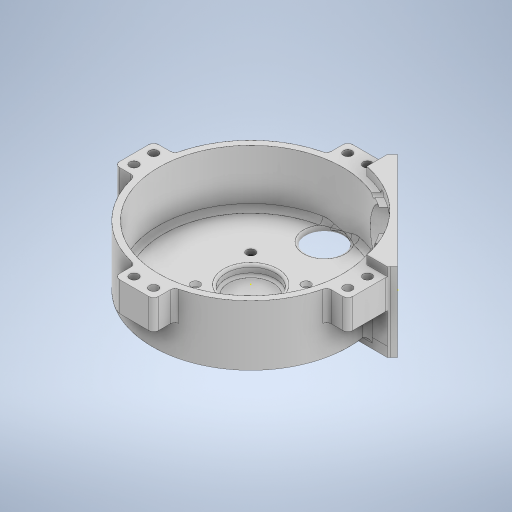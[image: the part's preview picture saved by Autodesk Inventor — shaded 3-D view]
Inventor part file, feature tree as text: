
AUTODESK INVENTOR PART (.ipt)
format: ipt  version: 2023 (Build 270158000, 158)  size: 803,840 bytes
history: native  units: in
note: dims shown in document units (in); Inventor stores cm internally (conversion verified against a paired STEP export)
features: sketch x26, extrude x21, fillet x11, hole x3
ambient origin geometry x8: Origin, YZ Plane, XZ Plane, XY Plane, X Axis, Y Axis, Z Axis, Center Point
bodies: Solid1 (feature_tree)
feature tree (61):
  extrude  "Extrusion1"  Depth=1.375in TaperAngle=0.0deg
  extrude  "Extrusion2"  Depth=1.275in TaperAngle=0.0deg
  extrude  "Extrusion3"  Depth=1.125in TaperAngle=0.0deg
  hole  "Hole1"  [1 undecoded]
  extrude  "Extrusion4"  Depth=0.4in
  extrude  "Extrusion5"  Depth=0.4in
  hole  "Hole2"  [1 undecoded]
  extrude  "Extrusion6"  Depth=0.4in
  sketch  "Sketch10"  dims[d26=0.8in d27=0.4in]
  extrude  "Extrusion7"  Depth=0.4in
  extrude  "Extrusion8"  Depth=0.8in
  extrude  "Extrusion9"  Depth=0.4in
  extrude  "Extrusion18"  Depth=0.75in TaperAngle=0.0deg
  extrude  "Extrusion19"  Depth=0.2in
  extrude  "Extrusion20"  Depth=0.2in
  extrude  "Extrusion21"  Depth=0.4in
  extrude  "Extrusion22"  Depth=0.2in
  extrude  "Extrusion23"  Depth=0.2in
  sketch  "Sketch34"  dims[d125=0.3in d126=0.3in]
  hole  "Hole6"  [1 undecoded]
  extrude  "Extrusion24"  Depth=2.0in TaperAngle=0.0deg
  fillet  "Fillet1"  Radius=2.0in
  fillet  "Fillet2"  Radius=0.3in
  fillet  "Fillet3"  Radius=0.3in
  fillet  "Fillet4"  Radius=0.3in
  fillet  "Fillet5"  Radius=0.3in
  fillet  "Fillet6"  Radius=0.1in
  fillet  "Fillet7"  Radius=0.1in
  fillet  "Fillet8"  Radius=0.175in
  fillet  "Fillet9"  Radius=0.2in
  fillet  "Fillet10"  Radius=1.0875in
  fillet  "Fillet11"  Radius=1.425in
  extrude  "Extrusion25"  Depth=0.5in
  extrude  "Extrusion11"  Depth=0.5in
  extrude  "Extrusion13"  Depth=0.3in
  extrude  "Extrusion14"  Depth=0.3in
  extrude  "Extrusion16"  Depth=1.225in TaperAngle=0.0deg
  sketch  "Sketch1"  dims[d0=4.0in d1=1.375in d2=0.0in]
  sketch  "Sketch2"  dims[d3=3.75in d4=1.275in d5=0.0in]
  sketch  "Sketch3"  dims[d6=1.0in d7=1.125in d8=0.0in]
  sketch  "Sketch4"  dims[d9=1.125in d10=1.125in]
  sketch  "Sketch5"  dims[d11=0.177in d12=0.75in d13=0.332in d14=0.25in d15=0.5635in d16=1.0in d17=0.8108in d18=0.4in]
  sketch  "Sketch6"  dims[d19=0.5in d20=0.4in]
  sketch  "Sketch7"  dims[d21=0.5in d22=0.75in d23=0.0in]
  sketch  "Sketch8"  dims[d24=0.5in d25=0.4in]
  sketch  "Sketch11"  dims[d28=0.5in d29=0.8in]
  sketch  "Sketch12"  dims[d30=0.5in d31=0.4in]
  sketch  "Sketch13"  dims[d32=0.8in d33=0.75in d34=0.0in]
  sketch  "Sketch17"  dims[d35=0.2in d36=0.2in]
  sketch  "Sketch19"  dims[d37=0.4in d38=0.2in]
  sketch  "Sketch20"  dims[d39=0.2in d40=0.4in]
  sketch  "Sketch23"  dims[d41=0.2in d42=0.2in]
  sketch  "Sketch26"  dims[d43=0.2in d44=0.2in]
  sketch  "Sketch27"  dims[d45=0.4in]
  sketch  "Sketch28"  dims[d46=0.177in d47=0.75in d48=0.375in d49=0.25in d50=0.5635in d51=0.75in d52=0.8108in d53=1.5in]
  sketch  "Sketch30"  dims[d54=0.75in d55=0.0in d66=0.15in d67=0.0in d68=2.0in d69=0.3in d70=0.3in d71=0.3in d72=0.3in d73=0.1in d74=0.0in d75=0.1in d76=0.0in d79=0.175in d80=0.0in d84=0.2in d85=0.0in d86=1.0875in d87=0.0in d101=1.425in d102=0.0in]
  sketch  "Sketch32"  dims[d105=0.3in d106=0.0in d122=0.5in]
  sketch  "Sketch33"  dims[d123=0.5in d124=0.5in]
  sketch  "Sketch35"  dims[d127=0.3in d128=0.3in]
  sketch  "Sketch36"  dims[d129=0.175in d130=1.225in d131=0.0in d132=0.0in d133=0.0625in d134=1.125in d135=0.0in d136=0.0in]
  sketch  "Sketch37"  dims[d137=0.15in d138=1.6in d139=0.0in d140=0.375in d141=0.0in d142=0.2in d143=0.0in d144=0.3in d145=0.2in d146=0.0in d147=0.8in d148=1.275in d149=1.275in d150=0.126in d151=0.75in d152=0.248in d153=0.25in d154=90.0deg d155=0.5in d156=0.8108in d157=1.5in d158=0.4in d159=0.0in d160=0.25in d161=0.25in d162=0.25in d163=0.1in d164=0.1in d165=0.1in d166=0.1in d167=0.05in d168=0.05in d169=0.1in d170=0.1in d171=0.175in d172=0.0in d81=0.5in d82=0.0344in]
note: 3 required parameter values undecoded (feature->parameter linkage not recoverable at this tier; creation-order binding heuristic only, values carry confidence <= 0.55)
